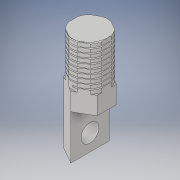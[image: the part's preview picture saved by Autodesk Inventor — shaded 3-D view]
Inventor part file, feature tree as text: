
AUTODESK INVENTOR PART (.ipt)
format: ipt  version: 2018 (Build 220112000, 112)  size: 555,008 bytes
history: native  units: in
note: dims shown in document units (in); Inventor stores cm internally (conversion verified against a paired STEP export)
features: sketch x5, extrude x3, hole x1, helix x1
ambient origin geometry x8: Origin, YZ Plane, XZ Plane, XY Plane, X Axis, Y Axis, Z Axis, Center Point
bodies: Solid1 (feature_tree)
feature tree (10):
  extrude  "Extrusion1"  TaperAngle=90.0deg  [1 undecoded]
  extrude  "Extrusion2"  Depth=1.2in TaperAngle=0.0deg
  hole  "Hole2"  [1 undecoded]
  extrude  "Extrusion3"  Depth=0.05in
  helix  "Coil1"  [1 undecoded]
  sketch  "Sketch1"  dims[d0=0.1875in d1=90.0deg]
  sketch  "Sketch3"  dims[d2=2.3622in d4=360.0deg d6=1.2in d7=0.0in]
  sketch  "Sketch5"  dims[d15=0.5in d16=0.0in d17=0.1875in]
  sketch  "Sketch8"  dims[d18=0.266in]
  sketch  "Sketch9"  dims[d19=0.201in d20=0.5in d21=0.507in d22=0.25in d23=0.5635in d24=1.0in d25=0.8108in d28=0.39in d29=0.5in d30=0.0in d31=0.72in d32=0.04in d33=30.0deg d34=0.04in d35=60.0deg d36=0.05in d37=1.0in d38=3.937in d39=0.0in d40=90.0deg d41=90.0deg d42=0.0in d43=0.0in]
note: 3 required parameter values undecoded (feature->parameter linkage not recoverable at this tier; creation-order binding heuristic only, values carry confidence <= 0.55)
